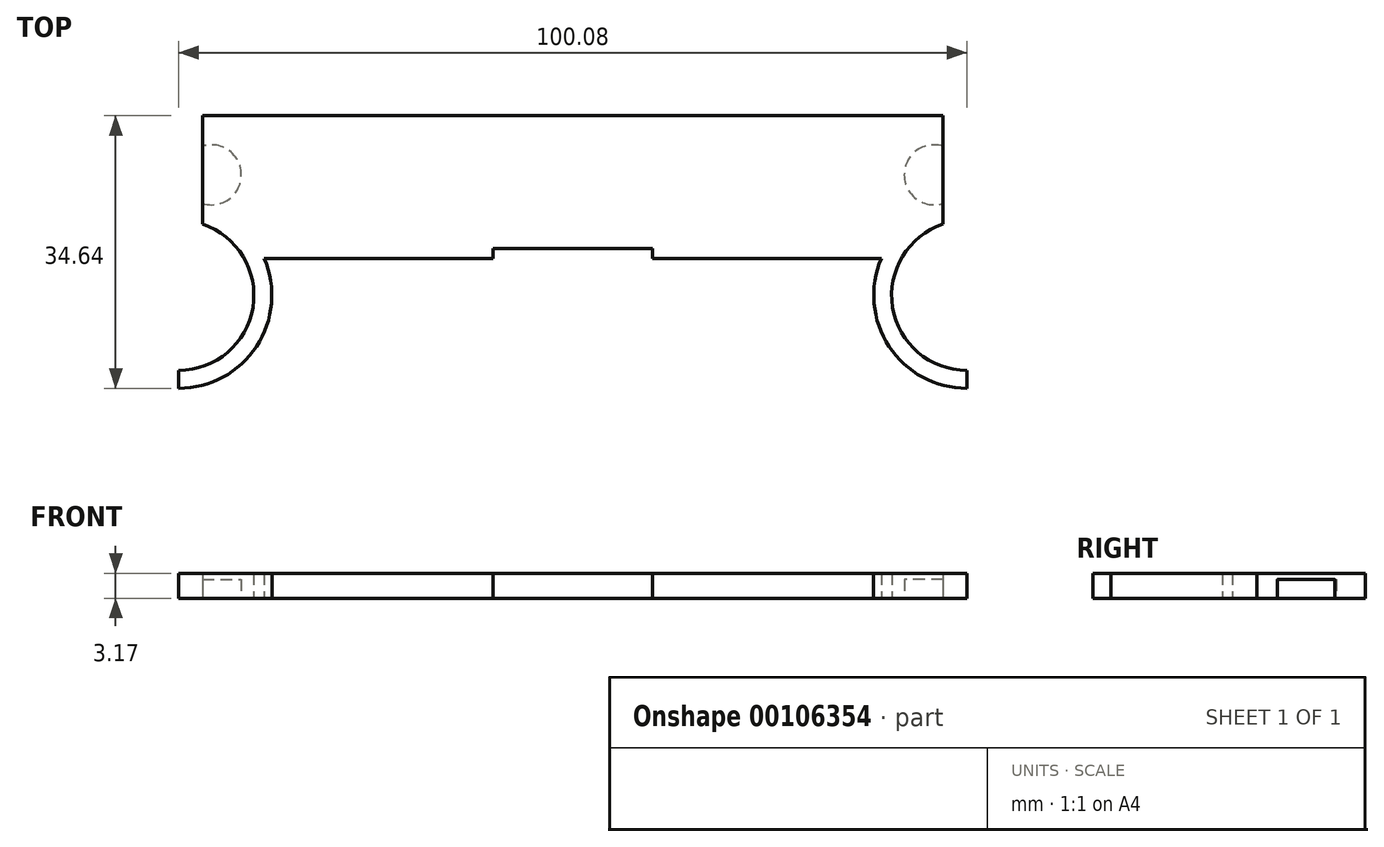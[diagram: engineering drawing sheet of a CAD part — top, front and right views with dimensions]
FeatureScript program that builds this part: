
annotation { "Feature Type Name" : "Feature", "Feature Type Description" : "" }
export const myFeature = defineFeature(function(context is Context, id is Id, definition is map)
    precondition{}
    {
        {
            var Q0;
            Q0=qCreatedBy(makeId("Top.planeOp"),FACE);
            var sketch = newSketch(context, id + "F0", { "sketchPlane" : qUnion([Q0])});
            skLineSegment(sketch, "E0.bottom", {"start": v(-47.04, 18.16) * mm, "end": v(47.04, 18.16) * mm});
            skLineSegment(sketch, "E0.top", {"start": v(-39.19, 0) * mm, "end": v(-10.16, 0) * mm});
            skLineSegment(sketch, "E0.left", {"start": v(-47.04, 18.16) * mm, "end": v(-47.04, 4.38) * mm});
            skLineSegment(sketch, "E0.right", {"start": v(47.04, 18.16) * mm, "end": v(47.04, 4.38) * mm});
            skArc(sketch, "E1", {"start": v(-50.04, -14.19) * mm, "mid": v(-40.63, -6.18) * mm, "end": v(-47.04, 4.38) * mm});
            skArc(sketch, "E2", {"start": v(-50.04, -16.48) * mm, "mid": v(-40.17, -11.16) * mm, "end": v(-39.19, 0) * mm});
            skLineSegment(sketch, "E3", {"start": v(-50.04, -14.19) * mm, "end": v(-50.04, -16.48) * mm});
            skArc(sketch, "E4.MirrorCS", {"start": v(50.04, -16.48) * mm, "mid": v(40.17, -11.16) * mm, "end": v(39.19, 0) * mm});
            skArc(sketch, "E5.MirrorCS", {"start": v(50.04, -14.19) * mm, "mid": v(40.63, -6.18) * mm, "end": v(47.04, 4.38) * mm});
            skLineSegment(sketch, "E6.MirrorCS", {"start": v(50.04, -14.19) * mm, "end": v(50.04, -16.48) * mm});
            skPoint(sketch, "E7.orphan", {"position": v(47.04, 0) * mm});
            skLineSegment(sketch, "E8.top", {"start": v(-10.16, 1.27) * mm, "end": v(10.16, 1.27) * mm});
            skLineSegment(sketch, "E8.left", {"start": v(-10.16, 0) * mm, "end": v(-10.16, 1.27) * mm});
            skLineSegment(sketch, "E8.right", {"start": v(10.16, 0) * mm, "end": v(10.16, 1.27) * mm});
            skLineSegment(sketch, "E9.trimOffspring", {"start": v(10.16, 0) * mm, "end": v(39.19, 0) * mm});
            skSolve(sketch);
        }
        {
            var Q0;
            Q0 = qSketchRegion(id + "F0", true);
            extrude(context, id + "F1", {"entities" : qUnion([Q0]), "depth" : 3.17 * mm});
        }
        {
            var Q0;
            Q0=makeQuery(id+"F1.opExtrude","CAP_FACE",FACE,{"disambiguationData":[OSD([sQuery(id+"F0.wireOp",EDGE,"E0.bottom"),sQuery(id+"F0.wireOp",EDGE,"E0.top"),sQuery(id+"F0.wireOp",EDGE,"E0.left"),sQuery(id+"F0.wireOp",EDGE,"E0.right"),sQuery(id+"F0.wireOp",EDGE,"E1"),sQuery(id+"F0.wireOp",EDGE,"E2"),sQuery(id+"F0.wireOp",EDGE,"E3"),sQuery(id+"F0.wireOp",EDGE,"E4.MirrorCS"),sQuery(id+"F0.wireOp",EDGE,"E5.MirrorCS"),sQuery(id+"F0.wireOp",EDGE,"E6.MirrorCS"),sQuery(id+"F0.wireOp",EDGE,"E8.top"),sQuery(id+"F0.wireOp",EDGE,"E8.left"),sQuery(id+"F0.wireOp",EDGE,"E8.right"),sQuery(id+"F0.wireOp",EDGE,"E9.trimOffspring")])],"isStart":true});
            var sketch = newSketch(context, id + "F2", { "sketchPlane" : qUnion([Q0])});
            skArc(sketch, "E10", {"start": v(-47.04, -14.28) * mm, "mid": v(-42.1, -10.64) * mm, "end": v(-47.04, -7) * mm});
            skLineSegment(sketch, "E11", {"start": v(-47.04, -7) * mm, "end": v(-47.04, -14.28) * mm});
            skArc(sketch, "E12.MirrorCS", {"start": v(47.04, -14.28) * mm, "mid": v(42.1, -10.64) * mm, "end": v(47.04, -7) * mm});
            skLineSegment(sketch, "E13.MirrorCS", {"start": v(47.04, -7) * mm, "end": v(47.04, -14.28) * mm});
            skSolve(sketch);
        }
        {
            var Q0;
            Q0 = qSketchRegion(id + "F2", true);
            extrude(context, id + "F3", {"entities" : qUnion([Q0]), "operationType" : NewBodyOperationType.REMOVE, "oppositeDirection" : true, "depth" : 2.41 * mm});
        }
    });
